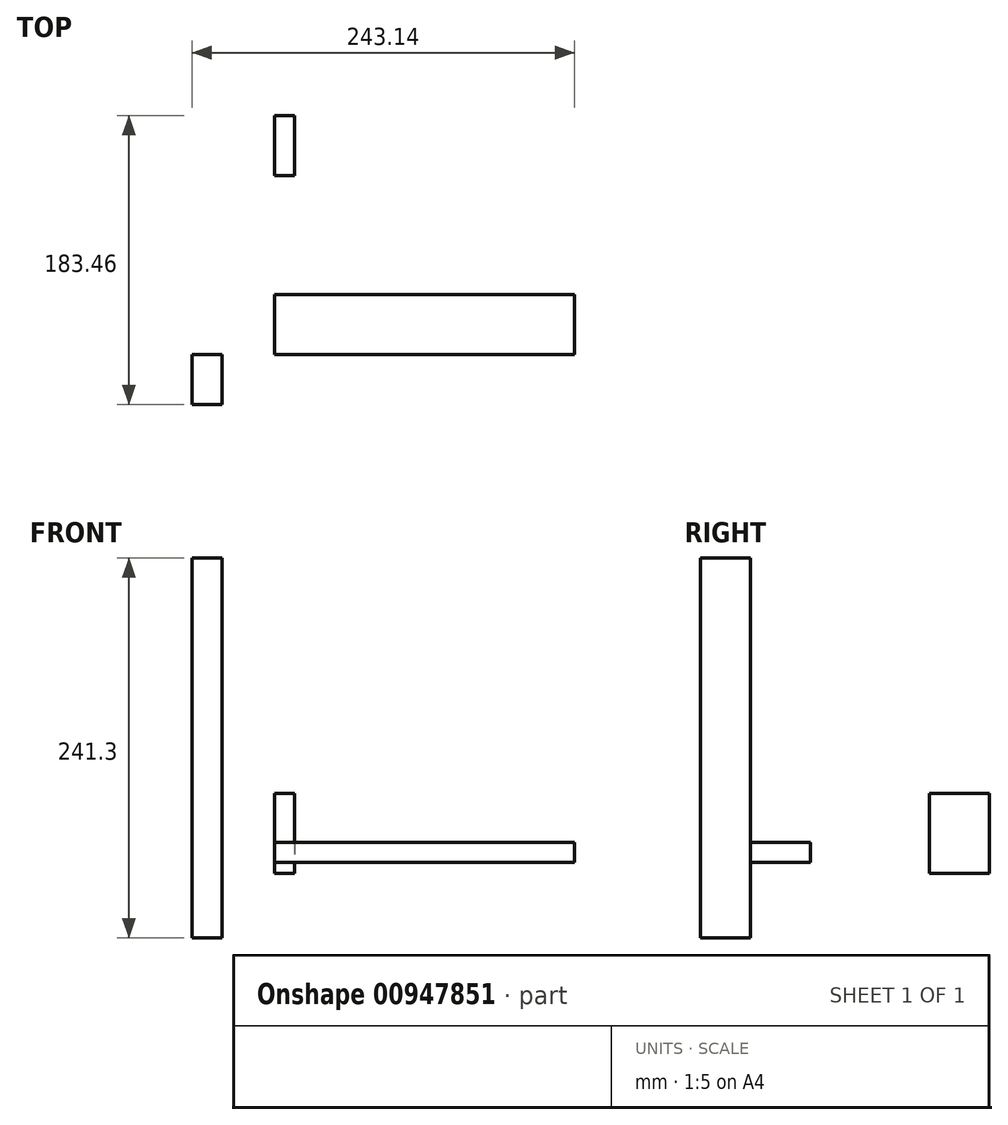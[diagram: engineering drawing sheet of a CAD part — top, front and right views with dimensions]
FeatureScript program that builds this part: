
annotation { "Feature Type Name" : "Feature", "Feature Type Description" : "" }
export const myFeature = defineFeature(function(context is Context, id is Id, definition is map)
    precondition{}
    {
        {
            var Q0;
            Q0=qCreatedBy(makeId("Front.planeOp"),FACE);
            var sketch = newSketch(context, id + "F0", { "sketchPlane" : qUnion([Q0])});
            skLineSegment(sketch, "E0.bottom", {"start": v(-52.64, 200.2) * mm, "end": v(-33.59, 200.2) * mm});
            skLineSegment(sketch, "E0.top", {"start": v(-52.64, -41.1) * mm, "end": v(-33.59, -41.1) * mm});
            skLineSegment(sketch, "E0.left", {"start": v(-52.64, 200.2) * mm, "end": v(-52.64, -41.1) * mm});
            skLineSegment(sketch, "E0.right", {"start": v(-33.59, 200.2) * mm, "end": v(-33.59, -41.1) * mm});
            skSolve(sketch);
        }
        {
            var Q0;
            Q0 = qSketchRegion(id + "F0", true);
            extrude(context, id + "F1", {"entities" : qUnion([Q0]), "depth" : 31.75 * mm, "offsetDistance" : 25.4 * mm});
        }
        {
            var Q0;
            Q0=qCreatedBy(makeId("Right.planeOp"),FACE);
            var sketch = newSketch(context, id + "F2", { "sketchPlane" : qUnion([Q0])});
            skLineSegment(sketch, "E1.bottom", {"start": v(0, 19.42) * mm, "end": v(38.1, 19.42) * mm});
            skLineSegment(sketch, "E1.top", {"start": v(0, 6.72) * mm, "end": v(38.1, 6.72) * mm});
            skLineSegment(sketch, "E1.left", {"start": v(0, 19.42) * mm, "end": v(0, 6.72) * mm});
            skLineSegment(sketch, "E1.right", {"start": v(38.1, 19.42) * mm, "end": v(38.1, 6.72) * mm});
            skSolve(sketch);
        }
        {
            var Q0;
            Q0=makeQuery(id+"F2.imprint","IMPRINT",FACE,{"disambiguationData":[TD([[makeQuery(id+"F2.imprint","IMPRINT",EDGE,{"derivedFrom":sQuery(id+"F2.wireOp",EDGE,"E1.bottom")}),-1.0]])]});
            extrude(context, id + "F3", {"entities" : qUnion([Q0]), "depth" : 190.5 * mm, "offsetDistance" : 25.4 * mm});
        }
        {
            var Q0;
            Q0=qCreatedBy(makeId("Top.planeOp"),FACE);
            var sketch = newSketch(context, id + "F4", { "sketchPlane" : qUnion([Q0])});
            skLineSegment(sketch, "E2.bottom", {"start": v(0, 151.7) * mm, "end": v(12.7, 151.7) * mm});
            skLineSegment(sketch, "E2.top", {"start": v(0, 113.6) * mm, "end": v(12.7, 113.6) * mm});
            skLineSegment(sketch, "E2.left", {"start": v(0, 151.7) * mm, "end": v(0, 113.6) * mm});
            skLineSegment(sketch, "E2.right", {"start": v(12.7, 151.7) * mm, "end": v(12.7, 113.6) * mm});
            skSolve(sketch);
        }
        {
            var Q0;
            Q0=makeQuery(id+"F4.imprint","IMPRINT",FACE,{"disambiguationData":[TD([[makeQuery(id+"F4.imprint","IMPRINT",EDGE,{"derivedFrom":sQuery(id+"F4.wireOp",EDGE,"E2.bottom")}),-1.0]])]});
            extrude(context, id + "F5", {"entities" : qUnion([Q0]), "depth" : 50.8 * mm, "offsetDistance" : 25.4 * mm});
        }
    });
